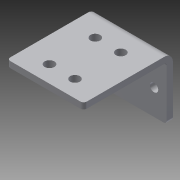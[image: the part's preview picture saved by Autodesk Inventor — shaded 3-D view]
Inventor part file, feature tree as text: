
AUTODESK INVENTOR PART (.ipt)
format: ipt  version: 2014 (Build 180170000, 170)  size: 137,728 bytes
history: native  units: in
note: dims shown in document units (in); Inventor stores cm internally (conversion verified against a paired STEP export)
features: sheet_metal_op x4, sketch x3, other x2, fillet x1, extrude x1
ambient origin geometry x8: Origin, YZ Plane, XZ Plane, XY Plane, X Axis, Y Axis, Z Axis, Center Point
bodies: Solid1 (feature_tree)
feature tree (11):
  sheet_metal_op  "Face1"
  sheet_metal_op  "Flange1"
  fillet  "Fillet1"  Radius=1.5in
  extrude  "Extrusion1"  Depth=0.163in
  sketch  "Sketch1"  dims[d1=1.0in d2=0.163in]
  other  "Plate1"
  sketch  "Sketch2"  dims[d3=0.25in]
  other  "Plate2"
  sheet_metal_op  "Bend1"
  sheet_metal_op  "Corner1"
  sketch  "Sketch3"  dims[d4=0.7874in d6=1.0in d7=0.3937in d9=1.0in d11=0.12in d12=0.12in d13=0.06in d14=0.24in d15=0.12in d16=1.75in d17=90.0deg d18=0.05in d19=0.48in d20=0.12in d21=0.12in d22=0.0625in d23=1.35in d24=0.75in d25=0.125in d26=0.375in d27=0.19in d28=0.125in d29=0.2265in d30=1.0in d31=0.0in]
